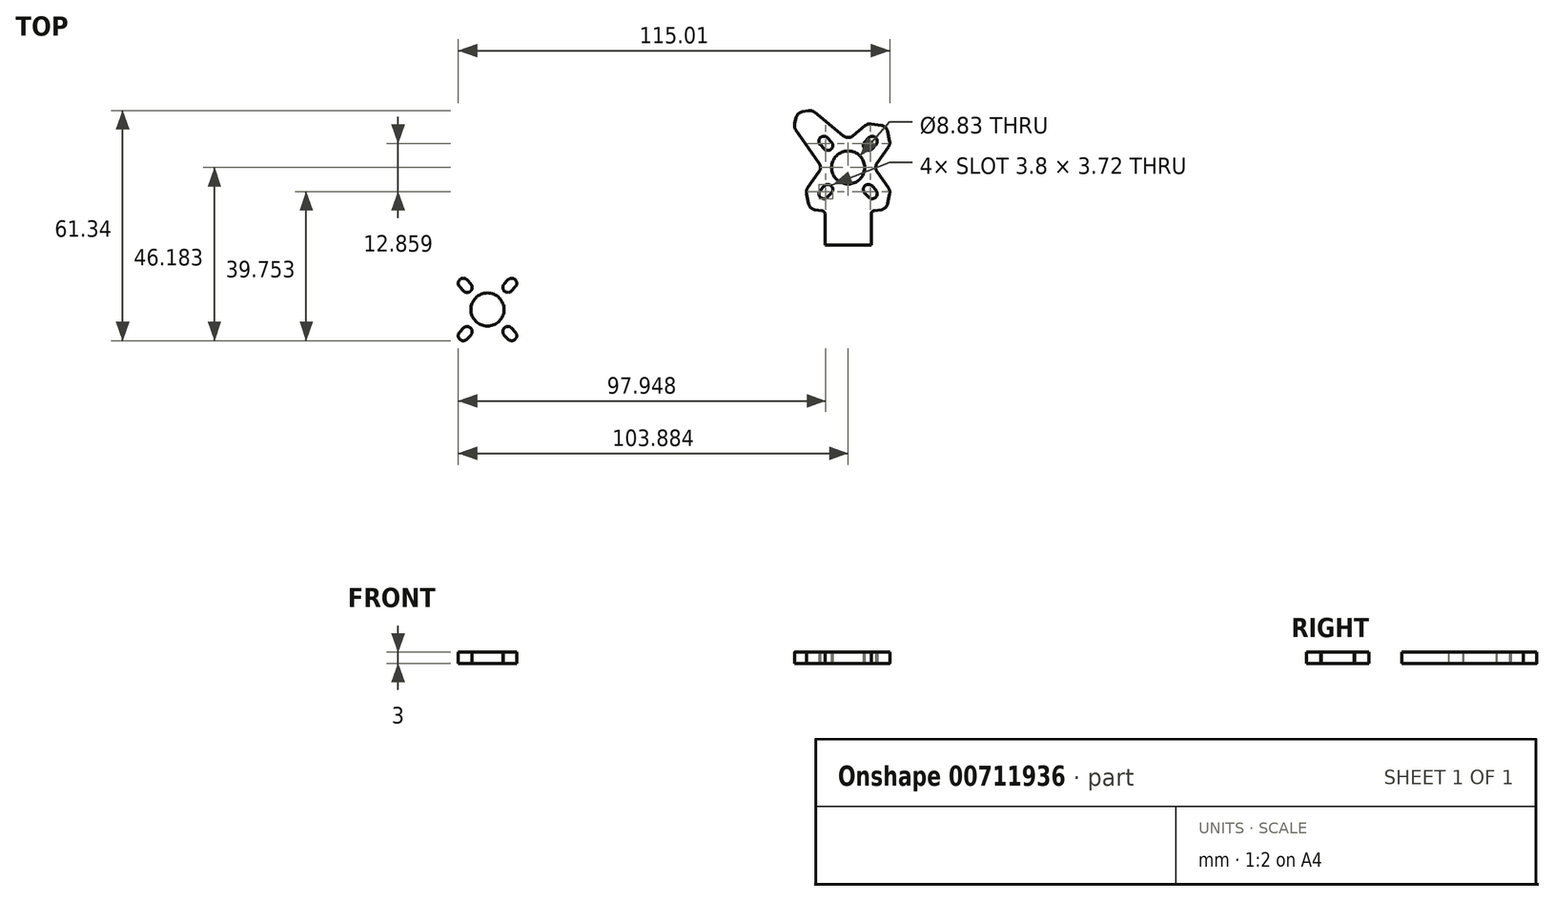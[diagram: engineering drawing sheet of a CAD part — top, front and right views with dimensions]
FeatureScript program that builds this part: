
annotation { "Feature Type Name" : "Feature", "Feature Type Description" : "" }
export const myFeature = defineFeature(function(context is Context, id is Id, definition is map)
    precondition{}
    {
        {
            var Q0;
            Q0=qCreatedBy(makeId("Top.planeOp"),FACE);
            var sketch = newSketch(context, id + "F0", { "sketchPlane" : qUnion([Q0])});
            skArc(sketch, "E0", {"start": v(33.27, 14.87) * mm, "mid": v(35.17, 14.79) * mm, "end": v(35.25, 16.7) * mm});
            skArc(sketch, "E1", {"start": v(34.23, 17.8) * mm, "mid": v(32.32, 17.88) * mm, "end": v(32.25, 15.97) * mm});
            skLineSegment(sketch, "E2", {"start": v(35.25, 16.7) * mm, "end": v(34.23, 17.8) * mm});
            skLineSegment(sketch, "E3.MirrorCS", {"start": v(33.27, 14.87) * mm, "end": v(32.25, 15.97) * mm});
            skArc(sketch, "E4.MirrorCS", {"start": v(46.38, 14.34) * mm, "mid": v(46.32, 14.29) * mm, "end": v(46.25, 14.24) * mm});
            skPoint(sketch, "E5.visualSharp", {"position": v(48.47, 17) * mm});
            skLineSegment(sketch, "E6", {"start": v(39.68, 9.9) * mm, "end": v(41.04, 9.85) * mm, "construction": true});
            skCircle(sketch, "E7", {"center": v(39.68, 9.9) * mm, "radius": 4.41 * mm});
            skPoint(sketch, "E8.visualSharp", {"position": v(31.14, 7.72) * mm});
            skPoint(sketch, "E9.visualSharp", {"position": v(34.72, 1.14) * mm});
            skLineSegment(sketch, "E10", {"start": v(39.68, 9.9) * mm, "end": v(39.68, -12.37) * mm, "construction": true});
            skPoint(sketch, "E11.orphan", {"position": v(44.65, -27.66) * mm});
            skPoint(sketch, "E12.orphan", {"position": v(34.72, -27.66) * mm});
            skPoint(sketch, "E13", {"position": v(52.97, 18.1) * mm});
            skLineSegment(sketch, "E14", {"start": v(33.24, 16.88) * mm, "end": v(34.26, 15.78) * mm, "construction": true});
            skLineSegment(sketch, "E15", {"start": v(33.24, 16.88) * mm, "end": v(22.64, 28.37) * mm, "construction": true});
            skLineSegment(sketch, "E16", {"start": v(30.92, 12.52) * mm, "end": v(25.74, 19.94) * mm});
            skPoint(sketch, "E17.start.orphan", {"position": v(30.11, 11.72) * mm});
            skLineSegment(sketch, "E18.MirrorCS", {"start": v(48.44, 12.52) * mm, "end": v(50.45, 15.4) * mm});
            skLineSegment(sketch, "E19.MirrorCS", {"start": v(47.04, 17.88) * mm, "end": v(56.73, 28.37) * mm, "construction": true});
            skPoint(sketch, "E20.orphan", {"position": v(51.4, 26.91) * mm});
            skPoint(sketch, "E21.MirrorCS.end.orphan", {"position": v(55.7, 22.93) * mm});
            skPoint(sketch, "E21.MirrorCS.start.orphan", {"position": v(56.04, 24.4) * mm});
            skLineSegment(sketch, "E22", {"start": v(29.17, 25.03) * mm, "end": v(27.47, 24.73) * mm});
            skLineSegment(sketch, "E23.MirrorCS", {"start": v(25.45, 21.59) * mm, "end": v(25.88, 23.26) * mm});
            skPoint(sketch, "E24.orphan", {"position": v(27.98, 26.91) * mm});
            skPoint(sketch, "E25.orphan", {"position": v(23.66, 22.93) * mm});
            skPoint(sketch, "E26.visualSharp", {"position": v(26.2, 24.51) * mm});
            skArc(sketch, "E26.filletArc", {"start": v(27.47, 24.73) * mm, "mid": v(26.46, 24.23) * mm, "end": v(25.88, 23.26) * mm});
            skPoint(sketch, "E27.visualSharp", {"position": v(30.08, 25.18) * mm});
            skArc(sketch, "E27.filletArc", {"start": v(30.79, 24.6) * mm, "mid": v(30.03, 24.99) * mm, "end": v(29.17, 25.03) * mm});
            skArc(sketch, "E28.filletArc", {"start": v(25.45, 21.59) * mm, "mid": v(25.42, 20.73) * mm, "end": v(25.74, 19.94) * mm});
            skArc(sketch, "E29.MirrorCS", {"start": v(46.1, 14.87) * mm, "mid": v(44.2, 14.79) * mm, "end": v(44.12, 16.7) * mm});
            skLineSegment(sketch, "E30.MirrorCS", {"start": v(44.12, 16.7) * mm, "end": v(45.14, 17.8) * mm});
            skArc(sketch, "E31.MirrorCS", {"start": v(45.14, 17.8) * mm, "mid": v(47.04, 17.88) * mm, "end": v(47.12, 15.97) * mm});
            skLineSegment(sketch, "E32.MirrorCS", {"start": v(46.1, 14.87) * mm, "end": v(47.12, 15.97) * mm});
            skArc(sketch, "E33.trimOffspring", {"start": v(44.5, 16.28) * mm, "mid": v(44.52, 16.3) * mm, "end": v(44.55, 16.33) * mm});
            skLineSegment(sketch, "E34", {"start": v(39.68, 9.9) * mm, "end": v(64.42, 9.9) * mm, "construction": true});
            skPoint(sketch, "E35.MirrorP", {"position": v(51.4, -7.1) * mm});
            skPoint(sketch, "E36.MirrorP", {"position": v(56.04, -4.6) * mm});
            skPoint(sketch, "E37.MirrorCS.end.orphan", {"position": v(49.26, 11.72) * mm});
            skLineSegment(sketch, "E38", {"start": v(45.83, 21.5) * mm, "end": v(48.5, 21.15) * mm});
            skLineSegment(sketch, "E39.MirrorCS", {"start": v(50.76, 16.96) * mm, "end": v(50.2, 19.6) * mm});
            skPoint(sketch, "E40.visualSharp", {"position": v(49.9, 20.97) * mm});
            skArc(sketch, "E40.filletArc", {"start": v(50.2, 19.6) * mm, "mid": v(49.6, 20.64) * mm, "end": v(48.5, 21.15) * mm});
            skPoint(sketch, "E41.orphan", {"position": v(46.92, 23.23) * mm});
            skPoint(sketch, "E42.orphan", {"position": v(52.4, 18.18) * mm});
            skPoint(sketch, "E43.visualSharp", {"position": v(44.97, 21.62) * mm});
            skArc(sketch, "E43.filletArc", {"start": v(45.83, 21.5) * mm, "mid": v(45.02, 21.45) * mm, "end": v(44.3, 21.07) * mm});
            skPoint(sketch, "E44.visualSharp", {"position": v(50.95, 16.1) * mm});
            skArc(sketch, "E44.filletArc", {"start": v(50.45, 15.4) * mm, "mid": v(50.77, 16.14) * mm, "end": v(50.76, 16.96) * mm});
            skPoint(sketch, "E45.MirrorP", {"position": v(52.97, 1.7) * mm});
            skPoint(sketch, "E46.MirrorP", {"position": v(52.4, 1.62) * mm});
            skArc(sketch, "E47.MirrorCS", {"start": v(44.5, 3.52) * mm, "mid": v(44.52, 3.5) * mm, "end": v(44.55, 3.48) * mm});
            skArc(sketch, "E48.MirrorCS", {"start": v(46.38, 5.46) * mm, "mid": v(46.32, 5.52) * mm, "end": v(46.25, 5.56) * mm});
            skArc(sketch, "E49.MirrorCS", {"start": v(50.45, 4.41) * mm, "mid": v(50.77, 3.66) * mm, "end": v(50.76, 2.85) * mm});
            skArc(sketch, "E50.MirrorCS", {"start": v(46.1, 4.94) * mm, "mid": v(44.2, 5.02) * mm, "end": v(44.12, 3.1) * mm});
            skLineSegment(sketch, "E51.MirrorCS", {"start": v(48.44, 7.29) * mm, "end": v(50.45, 4.41) * mm});
            skLineSegment(sketch, "E52.MirrorCS", {"start": v(46.1, 4.94) * mm, "end": v(47.12, 3.84) * mm});
            skPoint(sketch, "E53.MirrorP", {"position": v(48.47, 2.8) * mm});
            skPoint(sketch, "E54.MirrorP", {"position": v(49.9, -1.16) * mm});
            skArc(sketch, "E55.MirrorCS", {"start": v(45.14, 2) * mm, "mid": v(47.04, 1.93) * mm, "end": v(47.12, 3.84) * mm});
            skLineSegment(sketch, "E56.MirrorCS", {"start": v(46.7, -1.59) * mm, "end": v(48.5, -1.35) * mm});
            skLineSegment(sketch, "E57.MirrorCS", {"start": v(44.12, 3.1) * mm, "end": v(45.14, 2) * mm});
            skLineSegment(sketch, "E58.MirrorCS", {"start": v(50.76, 2.85) * mm, "end": v(50.2, 0.21) * mm});
            skPoint(sketch, "E59.MirrorP", {"position": v(50.95, 3.7) * mm});
            skPoint(sketch, "E60.MirrorP", {"position": v(49.26, 8.08) * mm});
            skArc(sketch, "E61.MirrorCS", {"start": v(50.2, 0.21) * mm, "mid": v(49.6, -0.83) * mm, "end": v(48.5, -1.35) * mm});
            skPoint(sketch, "E62.MirrorP", {"position": v(26.4, 1.7) * mm});
            skArc(sketch, "E63.MirrorCS", {"start": v(28.92, 4.41) * mm, "mid": v(28.6, 3.66) * mm, "end": v(28.6, 2.85) * mm});
            skPoint(sketch, "E64.MirrorP", {"position": v(26.97, 1.62) * mm});
            skPoint(sketch, "E65.MirrorP", {"position": v(30.9, 2.8) * mm});
            skPoint(sketch, "E66.MirrorP", {"position": v(30.11, 8.08) * mm});
            skArc(sketch, "E67.MirrorCS", {"start": v(29.17, 0.21) * mm, "mid": v(29.77, -0.83) * mm, "end": v(30.86, -1.35) * mm});
            skLineSegment(sketch, "E68.MirrorCS", {"start": v(35.25, 3.1) * mm, "end": v(34.23, 2) * mm});
            skLineSegment(sketch, "E69.MirrorCS", {"start": v(28.6, 2.85) * mm, "end": v(29.17, 0.21) * mm});
            skArc(sketch, "E70.MirrorCS", {"start": v(33.27, 4.94) * mm, "mid": v(35.17, 5.02) * mm, "end": v(35.25, 3.1) * mm});
            skArc(sketch, "E71.MirrorCS", {"start": v(34.23, 2) * mm, "mid": v(32.32, 1.93) * mm, "end": v(32.25, 3.84) * mm});
            skLineSegment(sketch, "E72.MirrorCS", {"start": v(30.92, 7.29) * mm, "end": v(28.92, 4.41) * mm});
            skPoint(sketch, "E73.MirrorP", {"position": v(29.47, -1.16) * mm});
            skPoint(sketch, "E74.MirrorP", {"position": v(28.42, 3.7) * mm});
            skLineSegment(sketch, "E75.MirrorCS", {"start": v(33.27, 4.94) * mm, "end": v(32.25, 3.84) * mm});
            skPoint(sketch, "E76.MirrorCS.end.orphan", {"position": v(33.11, 5.56) * mm});
            skPoint(sketch, "E76.MirrorCS.start.orphan", {"position": v(33, 5.46) * mm});
            skPoint(sketch, "E77.MirrorCS.end.orphan", {"position": v(34.82, 3.48) * mm});
            skPoint(sketch, "E77.MirrorCS.start.orphan", {"position": v(34.86, 3.52) * mm});
            skPoint(sketch, "E78.MirrorCS.start.orphan", {"position": v(37.77, 0.96) * mm});
            skPoint(sketch, "E79.MirrorCS.start.orphan", {"position": v(41.6, 0.96) * mm});
            skArc(sketch, "E80", {"start": v(-62.82, -22.98) * mm, "mid": v(-60.92, -23.06) * mm, "end": v(-60.84, -21.15) * mm});
            skArc(sketch, "E81", {"start": v(-61.86, -20.05) * mm, "mid": v(-63.77, -19.97) * mm, "end": v(-63.84, -21.88) * mm});
            skLineSegment(sketch, "E82", {"start": v(-60.84, -21.15) * mm, "end": v(-61.86, -20.05) * mm});
            skLineSegment(sketch, "E83.MirrorCS", {"start": v(-62.82, -22.98) * mm, "end": v(-63.84, -21.88) * mm});
            skArc(sketch, "E84.MirrorCS", {"start": v(-49.71, -23.5) * mm, "mid": v(-49.77, -23.56) * mm, "end": v(-49.84, -23.6) * mm});
            skPoint(sketch, "E85.visualSharp", {"position": v(-47.62, -20.84) * mm});
            skLineSegment(sketch, "E86", {"start": v(-56.4, -27.95) * mm, "end": v(-55.05, -28) * mm, "construction": true});
            skCircle(sketch, "E87", {"center": v(-56.4, -27.95) * mm, "radius": 4.41 * mm});
            skPoint(sketch, "E88.visualSharp", {"position": v(-64.95, -30.12) * mm});
            skPoint(sketch, "E89.visualSharp", {"position": v(-56.47, -19.1) * mm});
            skLineSegment(sketch, "E90", {"start": v(-61.37, -42.62) * mm, "end": v(-61.37, -51.9) * mm});
            skPoint(sketch, "E91.visualSharp", {"position": v(-61.37, -36.7) * mm});
            skLineSegment(sketch, "E92", {"start": v(-56.4, -27.95) * mm, "end": v(-56.4, -50.22) * mm, "construction": true});
            skLineSegment(sketch, "E93.MirrorCS", {"start": v(-51.44, -40.57) * mm, "end": v(-51.44, -51.9) * mm});
            skLineSegment(sketch, "E94", {"start": v(-51.44, -51.9) * mm, "end": v(-61.37, -51.9) * mm});
            skPoint(sketch, "E95.orphan", {"position": v(-51.44, -65.51) * mm});
            skPoint(sketch, "E96.orphan", {"position": v(-61.37, -65.51) * mm});
            skPoint(sketch, "E97", {"position": v(-43.12, -19.75) * mm});
            skLineSegment(sketch, "E98", {"start": v(-62.85, -20.97) * mm, "end": v(-61.83, -22.07) * mm, "construction": true});
            skLineSegment(sketch, "E99", {"start": v(-62.85, -20.97) * mm, "end": v(-73.45, -9.48) * mm, "construction": true});
            skLineSegment(sketch, "E100", {"start": v(-65.17, -25.33) * mm, "end": v(-70.35, -17.9) * mm});
            skPoint(sketch, "E101.start.orphan", {"position": v(-65.98, -26.12) * mm});
            skLineSegment(sketch, "E102.MirrorCS", {"start": v(-58.32, -19) * mm, "end": v(-65.3, -13.25) * mm});
            skLineSegment(sketch, "E103.MirrorCS", {"start": v(-54.5, -19) * mm, "end": v(-51.8, -16.78) * mm});
            skLineSegment(sketch, "E104.MirrorCS", {"start": v(-47.65, -25.33) * mm, "end": v(-45.64, -22.46) * mm});
            skLineSegment(sketch, "E105.MirrorCS", {"start": v(-49.05, -19.97) * mm, "end": v(-39.36, -9.48) * mm, "construction": true});
            skArc(sketch, "E106", {"start": v(-58.32, -19) * mm, "mid": v(-56.4, -19.69) * mm, "end": v(-54.5, -19) * mm});
            skPoint(sketch, "E107.orphan", {"position": v(-44.7, -10.94) * mm});
            skPoint(sketch, "E108.MirrorCS.end.orphan", {"position": v(-40.39, -14.92) * mm});
            skPoint(sketch, "E108.MirrorCS.start.orphan", {"position": v(-40.05, -13.44) * mm});
            skLineSegment(sketch, "E109", {"start": v(-66.92, -12.82) * mm, "end": v(-68.62, -13.12) * mm});
            skLineSegment(sketch, "E110.MirrorCS", {"start": v(-70.64, -16.26) * mm, "end": v(-70.21, -14.6) * mm});
            skPoint(sketch, "E111.orphan", {"position": v(-68.11, -10.94) * mm});
            skPoint(sketch, "E112.orphan", {"position": v(-72.43, -14.92) * mm});
            skPoint(sketch, "E113.visualSharp", {"position": v(-69.9, -13.34) * mm});
            skArc(sketch, "E113.filletArc", {"start": v(-68.62, -13.12) * mm, "mid": v(-69.63, -13.62) * mm, "end": v(-70.21, -14.6) * mm});
            skPoint(sketch, "E114.visualSharp", {"position": v(-66.01, -12.67) * mm});
            skArc(sketch, "E114.filletArc", {"start": v(-65.3, -13.25) * mm, "mid": v(-66.06, -12.86) * mm, "end": v(-66.92, -12.82) * mm});
            skPoint(sketch, "E115.visualSharp", {"position": v(-70.87, -17.15) * mm});
            skArc(sketch, "E115.filletArc", {"start": v(-70.64, -16.26) * mm, "mid": v(-70.67, -17.12) * mm, "end": v(-70.35, -17.9) * mm});
            skArc(sketch, "E116.MirrorCS", {"start": v(-49.99, -22.98) * mm, "mid": v(-51.9, -23.06) * mm, "end": v(-51.97, -21.15) * mm});
            skLineSegment(sketch, "E117.MirrorCS", {"start": v(-51.97, -21.15) * mm, "end": v(-50.95, -20.05) * mm});
            skArc(sketch, "E118.MirrorCS", {"start": v(-50.95, -20.05) * mm, "mid": v(-49.05, -19.97) * mm, "end": v(-48.97, -21.88) * mm});
            skLineSegment(sketch, "E119.MirrorCS", {"start": v(-49.99, -22.98) * mm, "end": v(-48.97, -21.88) * mm});
            skArc(sketch, "E120.trimOffspring", {"start": v(-51.59, -21.56) * mm, "mid": v(-51.57, -21.54) * mm, "end": v(-51.54, -21.52) * mm});
            skLineSegment(sketch, "E121", {"start": v(-56.4, -27.95) * mm, "end": v(-31.67, -27.95) * mm, "construction": true});
            skPoint(sketch, "E122.MirrorP", {"position": v(-44.7, -44.95) * mm});
            skPoint(sketch, "E123.MirrorP", {"position": v(-40.05, -42.45) * mm});
            skPoint(sketch, "E124.MirrorCS.start.orphan", {"position": v(-51.44, -42.62) * mm});
            skPoint(sketch, "E125.MirrorCS.end.orphan", {"position": v(-46.83, -26.12) * mm});
            skLineSegment(sketch, "E126", {"start": v(-50.26, -16.34) * mm, "end": v(-47.59, -16.7) * mm});
            skLineSegment(sketch, "E127.MirrorCS", {"start": v(-45.33, -20.9) * mm, "end": v(-45.9, -18.26) * mm});
            skPoint(sketch, "E128.visualSharp", {"position": v(-46.2, -16.88) * mm});
            skArc(sketch, "E128.filletArc", {"start": v(-45.9, -18.26) * mm, "mid": v(-46.5, -17.2) * mm, "end": v(-47.59, -16.7) * mm});
            skPoint(sketch, "E129.orphan", {"position": v(-49.17, -14.61) * mm});
            skPoint(sketch, "E130.orphan", {"position": v(-43.7, -19.66) * mm});
            skPoint(sketch, "E131.visualSharp", {"position": v(-51.12, -16.22) * mm});
            skArc(sketch, "E131.filletArc", {"start": v(-50.26, -16.34) * mm, "mid": v(-51.07, -16.4) * mm, "end": v(-51.8, -16.78) * mm});
            skPoint(sketch, "E132.visualSharp", {"position": v(-45.14, -21.74) * mm});
            skArc(sketch, "E132.filletArc", {"start": v(-45.64, -22.46) * mm, "mid": v(-45.32, -21.7) * mm, "end": v(-45.33, -20.9) * mm});
            skPoint(sketch, "E133.MirrorP", {"position": v(-43.12, -36.14) * mm});
            skPoint(sketch, "E134.MirrorP", {"position": v(-43.7, -36.23) * mm});
            skArc(sketch, "E135.MirrorCS", {"start": v(-51.59, -34.33) * mm, "mid": v(-51.57, -34.35) * mm, "end": v(-51.54, -34.37) * mm});
            skArc(sketch, "E136.MirrorCS", {"start": v(-49.71, -32.38) * mm, "mid": v(-49.77, -32.33) * mm, "end": v(-49.84, -32.28) * mm});
            skArc(sketch, "E137.MirrorCS", {"start": v(-45.64, -33.43) * mm, "mid": v(-45.32, -34.18) * mm, "end": v(-45.33, -35) * mm});
            skArc(sketch, "E138.MirrorCS", {"start": v(-50.26, -39.55) * mm, "mid": v(-50.36, -39.56) * mm, "end": v(-50.47, -39.57) * mm});
            skArc(sketch, "E139.MirrorCS", {"start": v(-49.99, -32.9) * mm, "mid": v(-51.9, -32.83) * mm, "end": v(-51.97, -34.74) * mm});
            skLineSegment(sketch, "E140.MirrorCS", {"start": v(-47.65, -30.56) * mm, "end": v(-45.64, -33.43) * mm});
            skLineSegment(sketch, "E141.MirrorCS", {"start": v(-49.99, -32.9) * mm, "end": v(-48.97, -34.01) * mm});
            skPoint(sketch, "E142.MirrorP", {"position": v(-47.62, -35.05) * mm});
            skPoint(sketch, "E143.MirrorP", {"position": v(-46.2, -39) * mm});
            skArc(sketch, "E144.MirrorCS", {"start": v(-50.95, -35.84) * mm, "mid": v(-49.05, -35.92) * mm, "end": v(-48.97, -34.01) * mm});
            skPoint(sketch, "E145.MirrorP", {"position": v(-51.12, -39.67) * mm});
            skLineSegment(sketch, "E146.MirrorCS", {"start": v(-50.26, -39.55) * mm, "end": v(-47.59, -39.2) * mm});
            skLineSegment(sketch, "E147.MirrorCS", {"start": v(-51.97, -34.74) * mm, "end": v(-50.95, -35.84) * mm});
            skLineSegment(sketch, "E148.MirrorCS", {"start": v(-45.33, -35) * mm, "end": v(-45.9, -37.63) * mm});
            skPoint(sketch, "E149.MirrorP", {"position": v(-45.14, -34.15) * mm});
            skPoint(sketch, "E150.MirrorP", {"position": v(-46.83, -29.77) * mm});
            skArc(sketch, "E151.MirrorCS", {"start": v(-45.9, -37.63) * mm, "mid": v(-46.5, -38.68) * mm, "end": v(-47.59, -39.2) * mm});
            skPoint(sketch, "E152.MirrorP", {"position": v(-69.7, -36.14) * mm});
            skArc(sketch, "E153.MirrorCS", {"start": v(-62.55, -39.55) * mm, "mid": v(-62.45, -39.56) * mm, "end": v(-62.34, -39.57) * mm});
            skArc(sketch, "E154.MirrorCS", {"start": v(-67.17, -33.43) * mm, "mid": v(-67.49, -34.18) * mm, "end": v(-67.48, -35) * mm});
            skPoint(sketch, "E155.MirrorP", {"position": v(-69.12, -36.23) * mm});
            skPoint(sketch, "E156.MirrorP", {"position": v(-65.2, -35.05) * mm});
            skPoint(sketch, "E157.MirrorP", {"position": v(-65.98, -29.77) * mm});
            skLineSegment(sketch, "E158.MirrorCS", {"start": v(-62.55, -39.55) * mm, "end": v(-65.23, -39.2) * mm});
            skArc(sketch, "E159.MirrorCS", {"start": v(-66.92, -37.63) * mm, "mid": v(-66.32, -38.68) * mm, "end": v(-65.23, -39.2) * mm});
            skLineSegment(sketch, "E160.MirrorCS", {"start": v(-60.84, -34.74) * mm, "end": v(-61.86, -35.84) * mm});
            skLineSegment(sketch, "E161.MirrorCS", {"start": v(-67.48, -35) * mm, "end": v(-66.92, -37.63) * mm});
            skArc(sketch, "E162.MirrorCS", {"start": v(-62.82, -32.9) * mm, "mid": v(-60.92, -32.83) * mm, "end": v(-60.84, -34.74) * mm});
            skPoint(sketch, "E163.MirrorP", {"position": v(-61.7, -39.67) * mm});
            skArc(sketch, "E164.MirrorCS", {"start": v(-61.86, -35.84) * mm, "mid": v(-63.77, -35.92) * mm, "end": v(-63.84, -34.01) * mm});
            skLineSegment(sketch, "E165.MirrorCS", {"start": v(-65.17, -30.56) * mm, "end": v(-67.17, -33.43) * mm});
            skPoint(sketch, "E166.MirrorP", {"position": v(-66.62, -39) * mm});
            skPoint(sketch, "E167.MirrorP", {"position": v(-67.67, -34.15) * mm});
            skLineSegment(sketch, "E168.MirrorCS", {"start": v(-61.37, -40.57) * mm, "end": v(-61.37, -51.9) * mm});
            skLineSegment(sketch, "E169.MirrorCS", {"start": v(-62.82, -32.9) * mm, "end": v(-63.84, -34.01) * mm});
            skPoint(sketch, "E170.MirrorCS.end.orphan", {"position": v(-62.98, -32.28) * mm});
            skPoint(sketch, "E170.MirrorCS.start.orphan", {"position": v(-63.1, -32.38) * mm});
            skPoint(sketch, "E171.MirrorCS.end.orphan", {"position": v(-61.27, -34.37) * mm});
            skPoint(sketch, "E171.MirrorCS.start.orphan", {"position": v(-61.23, -34.33) * mm});
            skPoint(sketch, "E172.MirrorCS.start.orphan", {"position": v(-58.32, -36.89) * mm});
            skPoint(sketch, "E173.MirrorCS.start.orphan", {"position": v(-54.5, -36.89) * mm});
            skPoint(sketch, "E174.orphan", {"position": v(-61.02, -39.11) * mm});
            skPoint(sketch, "E175.orphan", {"position": v(-61.37, -38.3) * mm});
            skPoint(sketch, "E176.orphan", {"position": v(-51.44, -38.3) * mm});
            skPoint(sketch, "E177.orphan", {"position": v(-51.8, -39.11) * mm});
            skPoint(sketch, "E178.visualSharp", {"position": v(-61.37, -39.34) * mm});
            skArc(sketch, "E178.filletArc", {"start": v(-61.37, -40.57) * mm, "mid": v(-61.65, -39.87) * mm, "end": v(-62.34, -39.57) * mm});
            skPoint(sketch, "E179.visualSharp", {"position": v(-51.44, -39.34) * mm});
            skArc(sketch, "E179.filletArc", {"start": v(-50.47, -39.57) * mm, "mid": v(-51.16, -39.87) * mm, "end": v(-51.44, -40.57) * mm});
            skArc(sketch, "E180.MirrorCS", {"start": v(-47.34, -29.14) * mm, "mid": v(-48.18, -27.29) * mm, "end": v(-47.65, -25.33) * mm});
            skPoint(sketch, "E181.startSnap0", {"position": v(-61.65, -39.87) * mm});
            skLineSegment(sketch, "E182", {"start": v(-62.04, -42.71) * mm, "end": v(-62.04, -49.14) * mm});
            skLineSegment(sketch, "E183.MirrorCS", {"start": v(-50.77, -42.71) * mm, "end": v(-50.77, -49.14) * mm});
            skLineSegment(sketch, "E184", {"start": v(-62.04, -42.71) * mm, "end": v(-62.04, -39.62) * mm});
            skLineSegment(sketch, "E185.MirrorCS", {"start": v(-50.77, -42.71) * mm, "end": v(-50.77, -39.62) * mm});
            skLineSegment(sketch, "E186", {"start": v(45.83, -2.58) * mm, "end": v(45.83, -10.84) * mm});
            skPoint(sketch, "E187.MirrorCS.end.orphan", {"position": v(45.32, -1.77) * mm});
            skPoint(sketch, "E187.MirrorCS.start.orphan", {"position": v(45.32, -4.87) * mm});
            skLineSegment(sketch, "E188.MirrorCS", {"start": v(33.54, -2.58) * mm, "end": v(33.54, -10.84) * mm});
            skLineSegment(sketch, "E189.MirrorCS", {"start": v(32.67, -1.59) * mm, "end": v(30.86, -1.35) * mm});
            skCircle(sketch, "E190", {"center": v(39.68, 9.9) * mm, "radius": 8 * mm, "construction": true});
            skCircle(sketch, "E191", {"center": v(39.68, 9.9) * mm, "radius": 9.5 * mm, "construction": true});
            skLineSegment(sketch, "E192", {"start": v(30.92, 12.52) * mm, "end": v(31.95, 11.05) * mm});
            skLineSegment(sketch, "E193", {"start": v(30.92, 7.29) * mm, "end": v(31.95, 8.76) * mm});
            skPoint(sketch, "E194.visualSharp", {"position": v(32.75, 9.9) * mm});
            skArc(sketch, "E194.filletArc", {"start": v(31.95, 8.76) * mm, "mid": v(32.31, 9.9) * mm, "end": v(31.95, 11.05) * mm});
            skPoint(sketch, "E195.orphan", {"position": v(48.44, 12.52) * mm});
            skPoint(sketch, "E196.MirrorCS.start.orphan", {"position": v(48.75, 8.71) * mm});
            skLineSegment(sketch, "E197.MirrorCS", {"start": v(48.44, 12.52) * mm, "end": v(47.42, 11.05) * mm});
            skLineSegment(sketch, "E198.MirrorCS", {"start": v(48.44, 7.29) * mm, "end": v(47.42, 8.76) * mm});
            skArc(sketch, "E199.MirrorCS", {"start": v(47.42, 8.76) * mm, "mid": v(47.06, 9.9) * mm, "end": v(47.42, 11.05) * mm});
            skLineSegment(sketch, "E200.MirrorCS", {"start": v(37.77, 18.84) * mm, "end": v(30.79, 24.6) * mm});
            skPoint(sketch, "E201.MirrorCS.start.orphan", {"position": v(41.6, 18.84) * mm});
            skLineSegment(sketch, "E202.MirrorCS", {"start": v(41.6, 18.84) * mm, "end": v(44.3, 21.07) * mm});
            skPoint(sketch, "E203.trimOffspring.end.orphan", {"position": v(48.58, 24.6) * mm});
            skPoint(sketch, "E204.visualSharp", {"position": v(39.68, 17.27) * mm});
            skLineSegment(sketch, "E205", {"start": v(37.77, 18.84) * mm, "end": v(38.41, 18.32) * mm});
            skLineSegment(sketch, "E206", {"start": v(41.6, 18.84) * mm, "end": v(40.96, 18.32) * mm});
            skArc(sketch, "E207.filletArc", {"start": v(38.41, 18.32) * mm, "mid": v(39.68, 17.86) * mm, "end": v(40.96, 18.32) * mm});
            skLineSegment(sketch, "E208", {"start": v(33.54, -10.84) * mm, "end": v(45.83, -10.84) * mm});
            skPoint(sketch, "E209.visualSharp", {"position": v(33.54, -1.7) * mm});
            skArc(sketch, "E209.filletArc", {"start": v(33.54, -2.58) * mm, "mid": v(33.29, -1.92) * mm, "end": v(32.67, -1.59) * mm});
            skPoint(sketch, "E210.visualSharp", {"position": v(45.83, -1.7) * mm});
            skArc(sketch, "E210.filletArc", {"start": v(46.7, -1.59) * mm, "mid": v(46.08, -1.92) * mm, "end": v(45.83, -2.58) * mm});
            skSolve(sketch);
        }
        {
            var Q0;
            Q0 = qSketchRegion(id + "F0", true);
            extrude(context, id + "F1", {"entities" : qUnion([Q0]), "depth" : 3 * mm, "offsetDistance" : 25 * mm});
        }
    });
